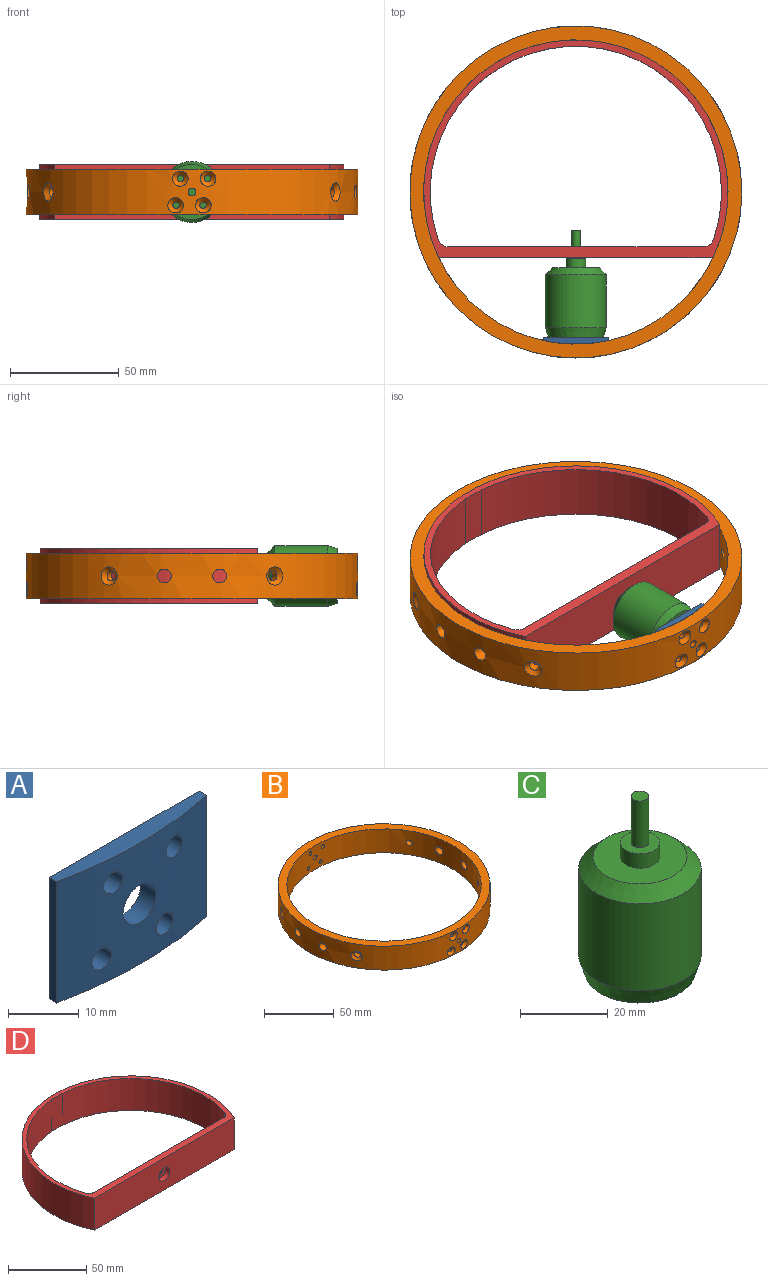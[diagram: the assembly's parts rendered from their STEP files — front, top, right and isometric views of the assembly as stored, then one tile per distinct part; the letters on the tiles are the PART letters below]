
ASSEMBLY  parts=4 mates=5
PART A: 11 faces, bbox 30x3.1x21 mm
  f0: plane 30x21mm, normal (0,1,0), area 558.3mm2, adj f1,f3,f4,f5,f6,f7,f8,f9
  f1: plane 21x1.5mm, normal (-1,0,0), area 31.5mm2, adj f0,f2,f4,f5
  f2: cylinder r=69.85mm len=30mm, axis (0,0,-1), area 563.1mm2, adj f1,f3,f4,f5,f6,f7,f8,f9
  f3: plane 21x1.5mm, normal (1,0,0), area 31.5mm2, adj f0,f2,f4,f5
  f4: plane 30x3.13mm, normal (0,0,1), area 77.7mm2, adj f0,f1,f2,f3
  f5: plane 30x3.13mm, normal (0,0,-1), area 77.7mm2, adj f0,f1,f2,f3
  f6: cylinder r=1.75mm len=3.5mm, axis (0,1,0), area 30.1mm2, adj f0,f2
  f7: cylinder r=1.75mm len=3.5mm, axis (0,1,0), area 32.2mm2, adj f0,f2
  f8: cylinder r=1.75mm len=3.5mm, axis (0,1,0), area 30.1mm2, adj f0,f2
  f9: cylinder r=1.75mm len=3.5mm, axis (0,1,0), area 32.2mm2, adj f0,f2
  f10: cylinder r=3.25mm len=6.5mm, axis (0,1,0), area 63.1mm2, adj f0,f2
PART B: 34 faces, bbox 152.4x152.4x21 mm
  f0: cylinder r=69.85mm len=139.7mm, axis (0,0,-1), area 8948.4mm2, adj f2,f3,f4,f5,f6,f7,f8,f9
  f1: cylinder r=76.2mm len=152.4mm, axis (0,0,-1), area 9365.3mm2, adj f2,f3,f12,f13,f14,f15,f16,f17
  f2: plane 152.4x152.4mm, normal (0,0,1), area 2913.6mm2, adj f0,f1
  f3: plane 152.4x152.4mm, normal (0,0,-1), area 2913.6mm2, adj f0,f1
  f4: cylinder r=1.5mm len=4.65mm, axis (0,1,0), area 40.8mm2, adj f0,f16
  f5: cylinder r=1.5mm len=4.65mm, axis (0,1,0), area 40.8mm2, adj f0,f21
  f6: cylinder r=1.5mm len=4.81mm, axis (0,1,0), area 40.9mm2, adj f0,f17
  f7: cylinder r=1.5mm len=4.81mm, axis (0,1,0), area 40.9mm2, adj f0,f20
  f8: cylinder r=1.5mm len=4.65mm, axis (0,1,0), area 40.8mm2, adj f0,f14
  f9: cylinder r=1.5mm len=4.65mm, axis (0,1,0), area 40.8mm2, adj f0,f19
  f10: cylinder r=1.5mm len=4.81mm, axis (0,1,0), area 40.9mm2, adj f0,f15
  f11: cylinder r=1.5mm len=4.81mm, axis (0,1,0), area 40.9mm2, adj f0,f18
  f12: cylinder r=1.75mm len=6.35mm, axis (0,1,0), area 69.8mm2, adj f0,f1
  f13: cylinder r=1.75mm len=6.35mm, axis (0,1,0), area 69.8mm2, adj f0,f1
  f14: bspline ~7.18x7mm, area 45.4mm2, adj f1,f8
  f15: bspline ~7.18x6.99mm, area 45.5mm2, adj f1,f10
  f16: bspline ~7.18x7mm, area 45.4mm2, adj f1,f4
  f17: bspline ~7.18x6.99mm, area 45.5mm2, adj f1,f6
  f18: bspline ~7.18x6.99mm, area 45.5mm2, adj f1,f11
  f19: bspline ~7.18x7mm, area 45.4mm2, adj f1,f9
  f20: bspline ~7.18x6.99mm, area 45.5mm2, adj f1,f7
  f21: bspline ~7.18x7mm, area 45.4mm2, adj f1,f5
  f22: cylinder r=2.25mm len=6.06mm, axis (-0.87,0.5,0), area 61.2mm2, adj f0,f28
  f23: cylinder r=2.25mm len=6.06mm, axis (-0.87,0.5,0), area 61.2mm2, adj f0,f27
  f24: cylinder r=2.25mm len=6.06mm, axis (0.87,0.5,0), area 61.2mm2, adj f0,f26
  f25: cylinder r=2.25mm len=6.06mm, axis (0.87,0.5,0), area 61.2mm2, adj f0,f29
  f26: bspline ~8.38x7.44mm, area 56.8mm2, adj f1,f24
  f27: bspline ~8.38x7.44mm, area 56.8mm2, adj f1,f23
  f28: bspline ~8.39x7.45mm, area 56.8mm2, adj f1,f22
  f29: bspline ~8.39x7.45mm, area 56.8mm2, adj f1,f25
  f30: cylinder r=3.17mm len=6.45mm, axis (1,0,0), area 128.6mm2, adj f0,f1
  f31: cylinder r=3.17mm len=6.45mm, axis (1,0,0), area 128.6mm2, adj f0,f1
  f32: cylinder r=3.17mm len=6.45mm, axis (1,0,0), area 128.6mm2, adj f0,f1
  f33: cylinder r=3.17mm len=6.45mm, axis (1,0,0), area 128.6mm2, adj f0,f1
PART C: 17 faces, bbox 28x28x49 mm
  f0: plane 25.25x25.25mm, normal (0,0,-1), area 472.5mm2, adj f1,f9,f11,f13,f15
  f1: cone r=12.62mm half-angle=17.3deg, axis (0,0,1), area 387.3mm2, adj f0,f2
  f2: cylinder r=14mm len=28mm, axis (0,0,-1), area 2135.8mm2, adj f1,f3
  f3: cone r=14mm half-angle=44.6deg, axis (0,0,-1), area 360mm2, adj f2,f4
  f4: plane 21.5x21.5mm, normal (0,0,1), area 299.4mm2, adj f3,f5
  f5: cylinder r=4.5mm len=9mm, axis (0,0,-1), area 113.1mm2, adj f4,f6
  f6: plane 9x9mm, normal (0,0,1), area 51.1mm2, adj f5,f7
  f7: cylinder r=2mm len=13mm, axis (0,0,-1), area 163.4mm2, adj f6,f8
  f8: plane 4x4mm, normal (0,0,1), area 12.6mm2, adj f7
  f9: cylinder r=1.5mm len=3mm, axis (0,0,-1), area 28.3mm2, adj f0,f10
  f10: plane 3x3mm, normal (0,0,-1), area 7.1mm2, adj f9
  f11: cylinder r=1.5mm len=3mm, axis (0,0,-1), area 28.3mm2, adj f0,f12
  f12: plane 3x3mm, normal (0,0,-1), area 7.1mm2, adj f11
  f13: cylinder r=1.5mm len=3mm, axis (0,0,-1), area 28.3mm2, adj f0,f14
  f14: plane 3x3mm, normal (0,0,-1), area 7.1mm2, adj f13
  f15: cylinder r=1.5mm len=3mm, axis (0,0,-1), area 28.3mm2, adj f0,f16
  f16: plane 3x3mm, normal (0,0,-1), area 7.1mm2, adj f15
PART D: 13 faces, bbox 139.7x100.1x25 mm
  f0: cylinder r=66.85mm len=88.52mm, axis (0,0,-1), area 3056.7mm2, adj f5,f6,f11,f12
  f1: cylinder r=69.85mm len=139.7mm, axis (0,0,-1), area 7048.6mm2, adj f4,f5,f6
  f2: plane 116.9x25mm, normal (0,1,0), area 2910mm2, adj f5,f6,f9,f10,f11
  f3: cylinder r=66.85mm len=88.52mm, axis (0,0,-1), area 3056.7mm2, adj f5,f6,f10,f12
  f4: plane 125.95x25mm, normal (0,-1,0), area 3070.2mm2, adj f1,f5,f6,f7
  f5: plane 139.7x100.07mm, normal (0,0,1), area 1445.8mm2, adj f0,f1,f2,f3,f4,f10,f11,f12
  f6: plane 139.7x100.07mm, normal (0,0,-1), area 1445.8mm2, adj f0,f1,f2,f3,f4,f10,f11,f12
  f7: cylinder r=5mm len=10mm, axis (0,-1,0), area 125.7mm2, adj f4,f8
  f8: plane 10x10mm, normal (0,-1,0), area 66mm2, adj f7,f9
  f9: cylinder r=2mm len=4mm, axis (0,-1,0), area 12.6mm2, adj f2,f8
  f10: cylinder r=5mm len=25mm, axis (0,0,-1), area 154.7mm2, adj f2,f3,f5,f6
  f11: cylinder r=5mm len=25mm, axis (0,0,-1), area 154.7mm2, adj f0,f2,f5,f6
  f12: plane 25x10mm, normal (0,-1,0), area 250mm2, adj f0,f3,f5,f6
PLACE A t=(-7.35,53.19,-4.81)mm
PLACE B t=(-7.35,53.19,-4.81)mm fixed
PLACE C rot(axis=(-0.89,-0.32,-0.32),96.8deg) t=(-7.35,-13.53,-4.81)mm
PLACE D t=(-7.35,53.19,-4.81)mm
MATE cylindrical C.f11 <-> B.f6  axis (0,-1,0) through (-0.08,-13.53,1.31)mm
MATE fastened B.f0 <-> A.f2  axis (0,0,1) through (-7.35,53.19,-4.81)mm
MATE planar A.f10 <-> C.f1  axis (0,1,0) through (-7.35,-13.53,-4.81)mm
MATE fastened D.f0 <-> A.f2  axis (0,0,1) through (-7.35,53.19,-4.81)mm
MATE cylindrical C.f15 <-> B.f10  axis (0,-1,0) through (-14.62,-13.53,-10.93)mm
